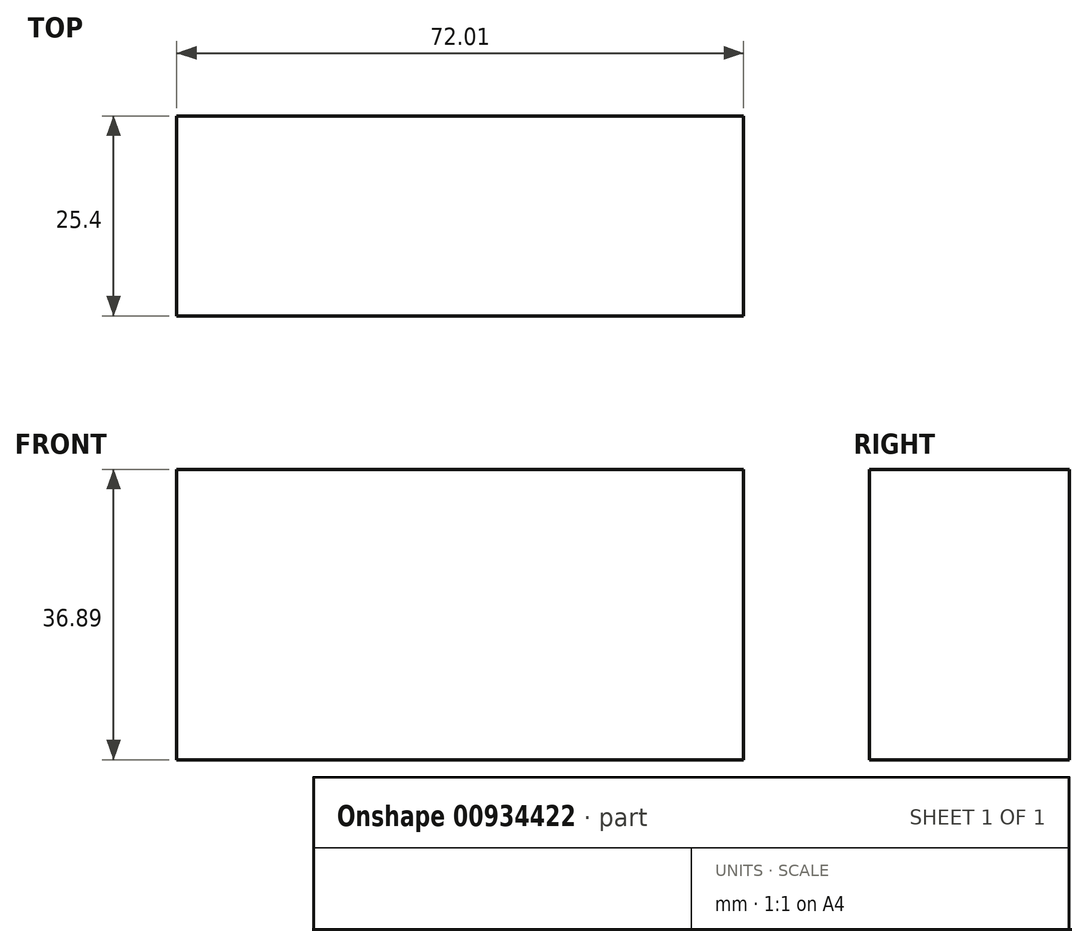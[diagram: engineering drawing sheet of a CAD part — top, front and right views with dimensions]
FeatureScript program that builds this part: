
annotation { "Feature Type Name" : "Feature", "Feature Type Description" : "" }
export const myFeature = defineFeature(function(context is Context, id is Id, definition is map)
    precondition{}
    {
        {
            var Q0;
            Q0=qCreatedBy(makeId("Front.planeOp"),FACE);
            var sketch = newSketch(context, id + "F0", { "sketchPlane" : qUnion([Q0])});
            skLineSegment(sketch, "E0.bottom", {"start": v(-35.7, 20.3) * mm, "end": v(36.3, 20.3) * mm});
            skLineSegment(sketch, "E0.top", {"start": v(-35.7, -16.6) * mm, "end": v(36.3, -16.6) * mm});
            skLineSegment(sketch, "E0.left", {"start": v(-35.7, 20.3) * mm, "end": v(-35.7, -16.6) * mm});
            skLineSegment(sketch, "E0.right", {"start": v(36.3, 20.3) * mm, "end": v(36.3, -16.6) * mm});
            skSolve(sketch);
        }
        {
            var Q0;
            Q0=makeQuery(id+"F0.imprint","IMPRINT",FACE,{"disambiguationData":[TD([[makeQuery(id+"F0.imprint","IMPRINT",EDGE,{"derivedFrom":sQuery(id+"F0.wireOp",EDGE,"E0.bottom")}),-1.0]])]});
            extrude(context, id + "F1", {"entities" : qUnion([Q0]), "depth" : 25.4 * mm, "offsetDistance" : 25.4 * mm});
        }
    });
